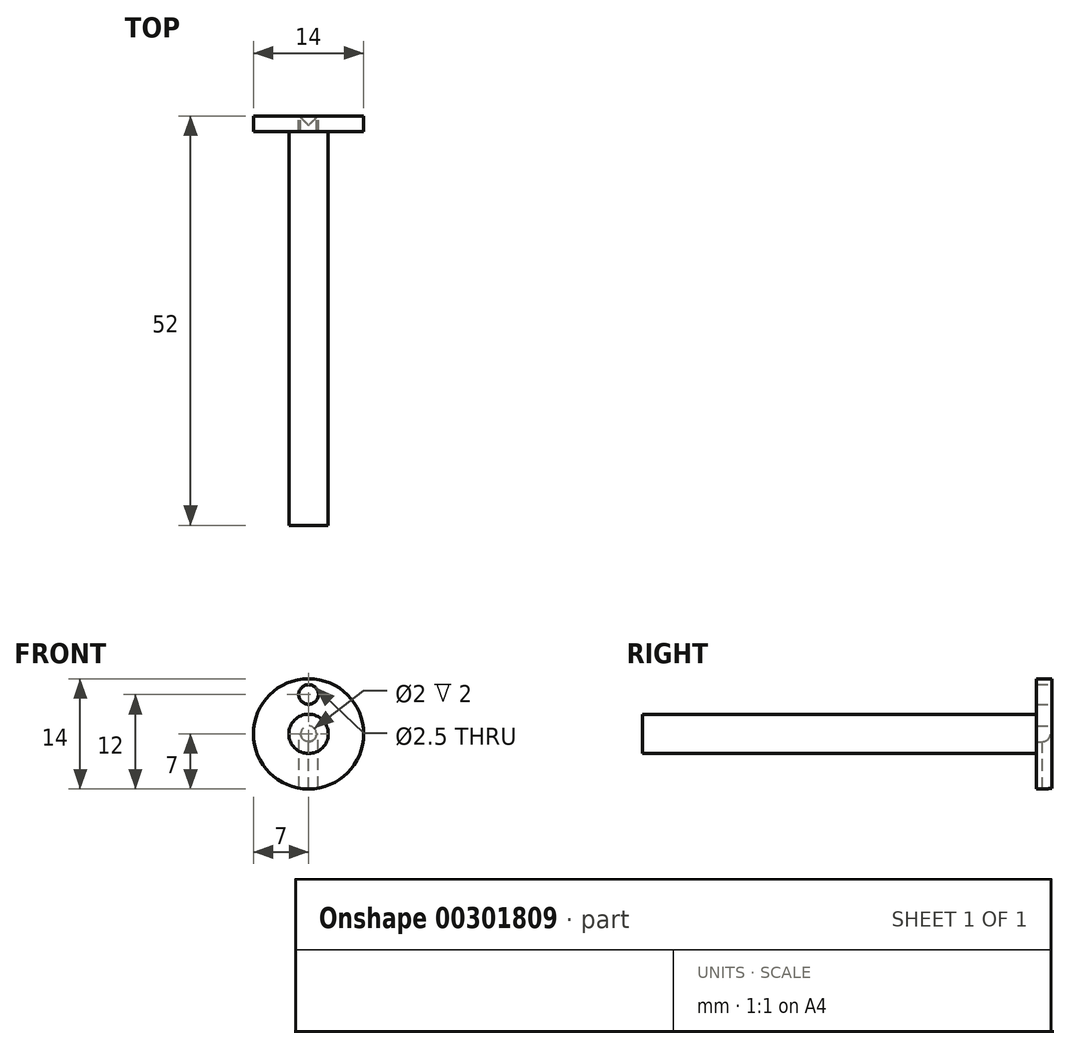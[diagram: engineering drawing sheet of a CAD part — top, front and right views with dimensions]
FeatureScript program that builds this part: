
annotation { "Feature Type Name" : "Feature", "Feature Type Description" : "" }
export const myFeature = defineFeature(function(context is Context, id is Id, definition is map)
    precondition{}
    {
        {
            var Q0;
            Q0=qCreatedBy(makeId("Front.planeOp"),FACE);
            var sketch = newSketch(context, id + "F0", { "sketchPlane" : qUnion([Q0])});
            skCircle(sketch, "E0", {"center": v(0, 0) * mm, "radius": 7 * mm});
            skCircle(sketch, "E1", {"center": v(0, 0) * mm, "radius": 1 * mm});
            skSolve(sketch);
        }
        {
            var Q0;
            Q0=qSketchRegion(id+"F0",true);
            extrude(context, id + "F1", {"entities" : qUnion([Q0]), "depth" : 2 * mm});
        }
        {
            var Q0;
            Q0=qCreatedBy(makeId("Top.planeOp"),FACE);
            var sketch = newSketch(context, id + "F2", { "sketchPlane" : qUnion([Q0])});
            skLineSegment(sketch, "E2", {"start": v(0, 0) * mm, "end": v(0, -1.2) * mm, "construction": true});
            skLineSegment(sketch, "E3", {"start": v(0, -1.2) * mm, "end": v(-1.2, 0) * mm});
            skLineSegment(sketch, "E4", {"start": v(-1.2, 0) * mm, "end": v(1.2, 0) * mm});
            skLineSegment(sketch, "E5", {"start": v(1.2, 0) * mm, "end": v(0, -1.2) * mm});
            skSolve(sketch);
        }
        {
            var Q0;
            Q0=makeQuery(id+"F2.imprint","IMPRINT",FACE,{"disambiguationData":[TD([[makeQuery(id+"F2.imprint","IMPRINT",EDGE,{"derivedFrom":sQuery(id+"F2.wireOp",EDGE,"E3")}),-1.0]])]});
            var Q1;
            Q1=sQuery(id+"F2.wireOp",EDGE,"E2");
            extrude(context, id + "F3", {"entities" : qUnion([Q0]), "operationType" : NewBodyOperationType.REMOVE, "surfaceEntities" : qUnion([Q1]), "oppositeDirection" : true, "depth" : 25 * mm});
        }
        {
            var Q0;
            {var subQ0=sQuery(id+"F0.wireOp",EDGE,"E0");var subQ2=sQuery(id+"F2.wireOp",EDGE,"E3");var subQ3=makeQuery(id+"FR7tKtxvbDhesbC_1.1.F3.opExtrude","SWEPT_FACE",FACE,{"disambiguationData":[OSD([subQ2])]});var subQ5=sQuery(id+"F0.wireOp",EDGE,"E1");var subQ6=makeQuery(id+"F1.opExtrude","SWEPT_FACE",FACE,{"disambiguationData":[OSD([subQ5])]});var subQ7=makeQuery(id+"F1.opExtrude","CAP_FACE",FACE,{"disambiguationData":[OSD([subQ0,subQ5])],"isStart":true});Q0=makeQuery(id+"FR7tKtxvbDhesbC_1.2.F3.boolean.opBoolean","SPLIT",FACE,{"disambiguationData":[TD([makeQuery(id+"FR7tKtxvbDhesbC_1.1.F3.boolean.opBoolean","COPY",FACE,{"derivedFrom":subQ3})])],"derivedFrom":makeQuery(id+"FR7tKtxvbDhesbC_1.1.F3.boolean.opBoolean","SPLIT",FACE,{"disambiguationData":[TD([subQ6])],"derivedFrom":subQ7})});}
            var sketch = newSketch(context, id + "F4", { "sketchPlane" : qUnion([Q0])});
            skLineSegment(sketch, "E6", {"start": v(0, 0) * mm, "end": v(0, 5) * mm, "construction": true});
            skCircle(sketch, "E7", {"center": v(0, 5) * mm, "radius": 1.25 * mm});
            skSolve(sketch);
        }
        {
            var Q0;
            Q0 = qSketchRegion(id + "F4", true);
            extrude(context, id + "F5", {"entities" : qUnion([Q0]), "operationType" : NewBodyOperationType.REMOVE, "endBound" : BoundingType.UP_TO_NEXT, "oppositeDirection" : true, "depth" : 25 * mm});
        }
        {
            var Q0;
            Q0=makeQuery(id+"F1.opExtrude","CAP_FACE",FACE,{"disambiguationData":[OSD([sQuery(id+"F0.wireOp",EDGE,"E0"),sQuery(id+"F0.wireOp",EDGE,"E1")])],"isStart":false});
            var sketch = newSketch(context, id + "F6", { "sketchPlane" : qUnion([Q0])});
            skCircle(sketch, "E8", {"center": v(0, 0) * mm, "radius": 2.5 * mm});
            skSolve(sketch);
        }
        {
            var Q0;
            Q0 = qSketchRegion(id + "F6", true);
            extrude(context, id + "F7", {"entities" : qUnion([Q0]), "operationType" : NewBodyOperationType.ADD, "depth" : 50 * mm});
        }
    });
